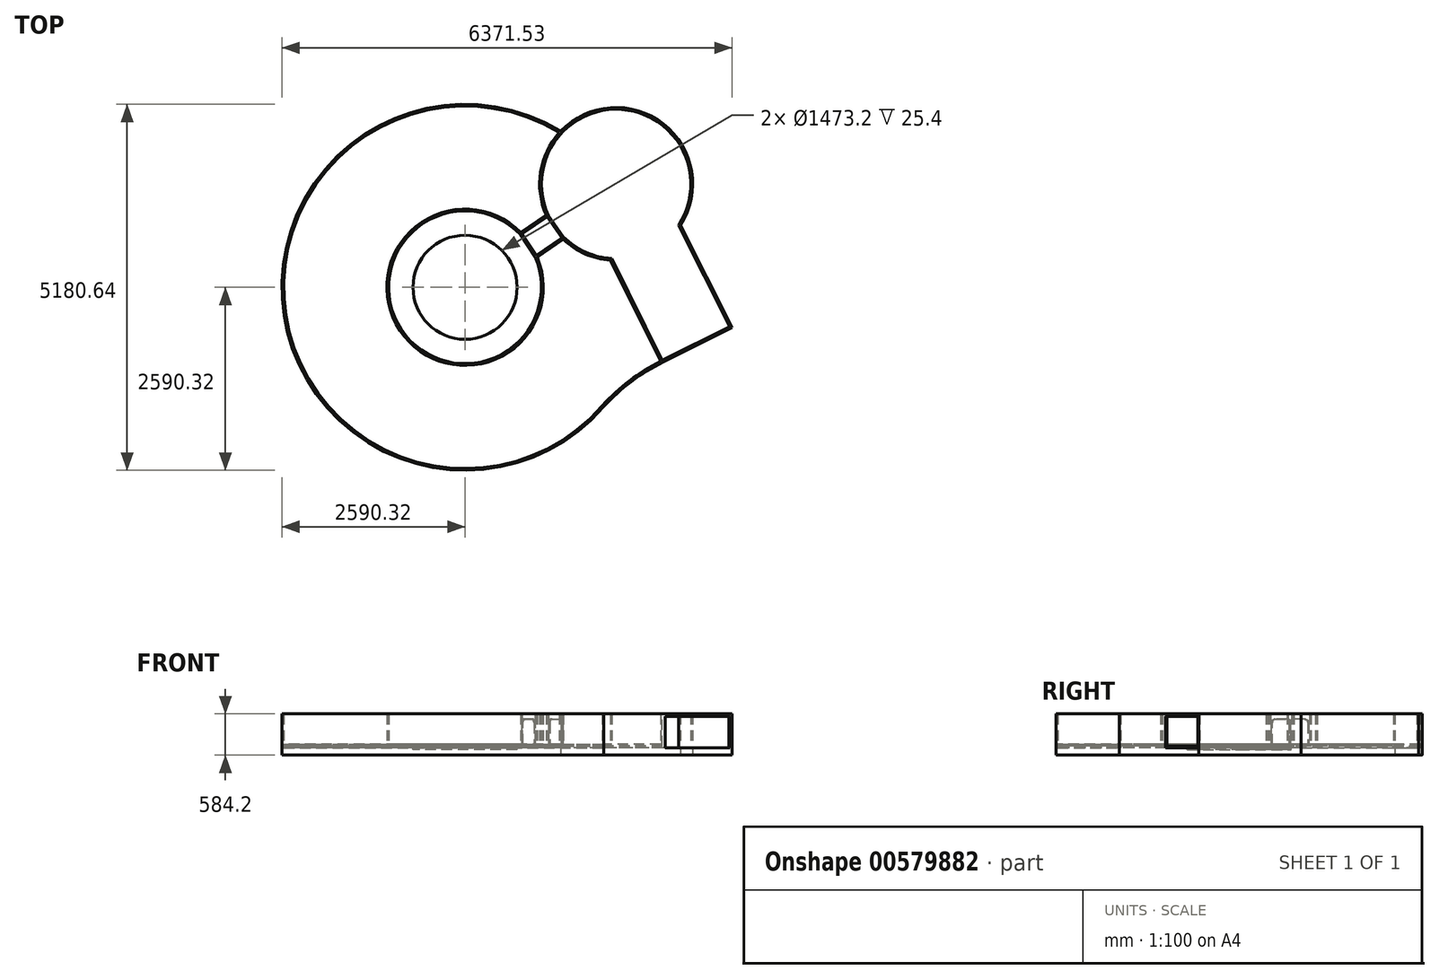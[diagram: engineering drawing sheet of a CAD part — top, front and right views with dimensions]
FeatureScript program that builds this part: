
annotation { "Feature Type Name" : "Feature", "Feature Type Description" : "" }
export const myFeature = defineFeature(function(context is Context, id is Id, definition is map)
    precondition{}
    {
        {
            var Q0;
            Q0=qCreatedBy(makeId("Top.planeOp"),FACE);
            var sketch = newSketch(context, id + "F0", { "sketchPlane" : qUnion([Q0])});
            skArc(sketch, "E0", {"start": v(1353.94, 2208.3) * mm, "mid": v(-2559.24, -400.08) * mm, "end": v(1963.3, -1689.73) * mm});
            skArc(sketch, "E1", {"start": v(1393.84, 711.58) * mm, "mid": v(1706.32, 497.31) * mm, "end": v(2074.27, 407) * mm});
            skLineSegment(sketch, "E2.0", {"start": v(2085.56, 384.25) * mm, "end": v(2789.38, -1035.12) * mm});
            skLineSegment(sketch, "E3.0", {"start": v(3031.93, 857.23) * mm, "end": v(3747.03, -556.58) * mm});
            skLineSegment(sketch, "E4", {"start": v(3781.21, -567.89) * mm, "end": v(2800.66, -1057.88) * mm});
            skArc(sketch, "E5", {"start": v(2800.66, -1057.88) * mm, "mid": v(2353, -1335.39) * mm, "end": v(1963.3, -1689.73) * mm});
            skCircle(sketch, "E6", {"center": v(0, 0) * mm, "radius": 762 * mm});
            skArc(sketch, "E7", {"start": v(786.05, 742.15) * mm, "mid": v(-901.05, -597.29) * mm, "end": v(989.68, 434.94) * mm});
            skLineSegment(sketch, "E8", {"start": v(-1106.44, 0) * mm, "end": v(-2564.92, 0) * mm});
            skLineSegment(sketch, "E9", {"start": v(0, 1106.44) * mm, "end": v(0, 2564.92) * mm});
            skLineSegment(sketch, "E10", {"start": v(0, -1106.44) * mm, "end": v(0, -2564.92) * mm});
            skLineSegment(sketch, "E11.0", {"start": v(1160.51, 998.22) * mm, "end": v(807.27, 756.66) * mm});
            skLineSegment(sketch, "E12.0", {"start": v(1372.87, 697.23) * mm, "end": v(1011, 449.54) * mm});
            skLineSegment(sketch, "E13", {"start": v(786.05, 742.15) * mm, "end": v(989.68, 434.94) * mm});
            skLineSegment(sketch, "E14", {"start": v(1181.48, 1012.56) * mm, "end": v(1393.84, 711.58) * mm});
            skArc(sketch, "E15.trimOffspring", {"start": v(3020.47, 879.9) * mm, "mid": v(2214.25, 2516.5) * mm, "end": v(1181.48, 1012.56) * mm});
            skLineSegment(sketch, "E16", {"start": v(2074.27, 407) * mm, "end": v(3020.47, 879.9) * mm});
            skCircle(sketch, "E17.0", {"center": v(0, 0) * mm, "radius": 736.6 * mm});
            skLineSegment(sketch, "E18.0", {"start": v(1149.48, 1021.44) * mm, "end": v(789.44, 775.24) * mm});
            skArc(sketch, "E18.1", {"start": v(3049.74, 878.31) * mm, "mid": v(2806.23, 2313.93) * mm, "end": v(1353.94, 2208.3) * mm});
            skLineSegment(sketch, "E19.0", {"start": v(1391.03, 678.87) * mm, "end": v(1021.24, 425.76) * mm});
            skArc(sketch, "E19.1", {"start": v(1391.03, 678.87) * mm, "mid": v(1698.8, 472.86) * mm, "end": v(2058, 382.64) * mm});
            skArc(sketch, "E20.1", {"start": v(2766.7, -1046.58) * mm, "mid": v(2327.45, -1322.88) * mm, "end": v(1944.3, -1672.87) * mm});
            skLineSegment(sketch, "E20.2", {"start": v(2058, 382.64) * mm, "end": v(2766.7, -1046.58) * mm});
            skLineSegment(sketch, "E21.0", {"start": v(3747.14, -556.52) * mm, "end": v(2789.3, -1035.16) * mm});
            skArc(sketch, "E22.trimOffspring", {"start": v(789.44, 775.24) * mm, "mid": v(-922.05, -611.58) * mm, "end": v(1021.24, 425.76) * mm});
            skLineSegment(sketch, "E23", {"start": v(807.27, 756.66) * mm, "end": v(1011, 449.54) * mm});
            skLineSegment(sketch, "E24.0", {"start": v(1160.73, 997.91) * mm, "end": v(1373.08, 696.93) * mm});
            skLineSegment(sketch, "E25", {"start": v(1160.73, 997.91) * mm, "end": v(1160.51, 998.22) * mm});
            skArc(sketch, "E26.trimOffspring", {"start": v(1336.3, 2189.32) * mm, "mid": v(-2533.72, -398.87) * mm, "end": v(1944.3, -1672.87) * mm});
            skArc(sketch, "E27.trimOffspring", {"start": v(1336.3, 2189.32) * mm, "mid": v(1069.3, 1633.15) * mm, "end": v(1149.48, 1021.44) * mm});
            skPoint(sketch, "E28.orphan", {"position": v(0, 1081.04) * mm});
            skPoint(sketch, "E29.orphan", {"position": v(-1081.04, 0) * mm});
            skPoint(sketch, "E30.orphan", {"position": v(0, -1081.04) * mm});
            skLineSegment(sketch, "E31.0", {"start": v(2085.63, 384.28) * mm, "end": v(3031.83, 857.18) * mm});
            skLineSegment(sketch, "E32", {"start": v(2085.63, 384.28) * mm, "end": v(2085.56, 384.25) * mm});
            skLineSegment(sketch, "E33", {"start": v(3031.83, 857.18) * mm, "end": v(3031.93, 857.23) * mm});
            skLineSegment(sketch, "E34", {"start": v(2766.7, -1046.58) * mm, "end": v(2789.38, -1035.12) * mm});
            skLineSegment(sketch, "E35", {"start": v(1181.48, 1012.56) * mm, "end": v(1149.48, 1021.44) * mm});
            skLineSegment(sketch, "E36", {"start": v(3049.74, 878.31) * mm, "end": v(3781.21, -567.89) * mm});
            skSolve(sketch);
        }
        {
            var Q0;
            Q0=makeQuery(id+"F0.imprint","IMPRINT",FACE,{"disambiguationData":[TD([[makeQuery(id+"F0.imprint","IMPRINT",EDGE,{"derivedFrom":sQuery(id+"F0.wireOp",EDGE,"E0")}),1.0]])]});
            var sketch = newSketch(context, id + "F1", { "sketchPlane" : qUnion([Q0])});
            skArc(sketch, "E37.0", {"start": v(1353.94, 2208.3) * mm, "mid": v(-2559.24, -400.08) * mm, "end": v(1963.3, -1689.73) * mm});
            skArc(sketch, "E38.0", {"start": v(2800.66, -1057.88) * mm, "mid": v(2353, -1335.39) * mm, "end": v(1963.3, -1689.73) * mm});
            skLineSegment(sketch, "E39.0", {"start": v(3781.21, -567.89) * mm, "end": v(2800.66, -1057.88) * mm});
            skLineSegment(sketch, "E40.0", {"start": v(3049.74, 878.31) * mm, "end": v(3781.21, -567.89) * mm});
            skArc(sketch, "E41.0", {"start": v(3049.74, 878.31) * mm, "mid": v(2806.23, 2313.93) * mm, "end": v(1353.94, 2208.3) * mm});
            skSolve(sketch);
        }
        {
            var Q0;
            Q0=makeQuery(id+"F0.imprint","IMPRINT",FACE,{"disambiguationData":[TD([[makeQuery(id+"F0.imprint","IMPRINT",EDGE,{"derivedFrom":sQuery(id+"F0.wireOp",EDGE,"E0")}),1.0]])]});
            var sketch = newSketch(context, id + "F2", { "sketchPlane" : qUnion([Q0])});
            skLineSegment(sketch, "E42.0.0", {"start": v(2800.66, -1057.88) * mm, "end": v(3781.21, -567.89) * mm});
            skLineSegment(sketch, "E42.0.1", {"start": v(3781.21, -567.89) * mm, "end": v(3049.74, 878.31) * mm});
            skArc(sketch, "E42.0.2", {"start": v(3049.74, 878.31) * mm, "mid": v(2806.23, 2313.93) * mm, "end": v(1353.94, 2208.3) * mm});
            skArc(sketch, "E42.0.3", {"start": v(1353.94, 2208.3) * mm, "mid": v(-2559.24, -400.08) * mm, "end": v(1963.3, -1689.73) * mm});
            skArc(sketch, "E42.0.4", {"start": v(1963.3, -1689.73) * mm, "mid": v(2353, -1335.39) * mm, "end": v(2800.66, -1057.88) * mm});
            skCircle(sketch, "E43.0.0", {"center": v(0, 0) * mm, "radius": 762 * mm});
            skCircle(sketch, "E44.0", {"center": v(0, 0) * mm, "radius": 736.6 * mm});
            skArc(sketch, "E45.0", {"start": v(786.05, 742.15) * mm, "mid": v(-901.05, -597.29) * mm, "end": v(989.68, 434.94) * mm});
            skArc(sketch, "E46.0", {"start": v(789.44, 775.24) * mm, "mid": v(-922.05, -611.58) * mm, "end": v(1021.24, 425.76) * mm});
            skLineSegment(sketch, "E47.0.0", {"start": v(1372.87, 697.23) * mm, "end": v(1160.73, 997.91) * mm});
            skLineSegment(sketch, "E47.0.1", {"start": v(1160.73, 997.91) * mm, "end": v(1160.51, 998.22) * mm});
            skLineSegment(sketch, "E47.0.2", {"start": v(1160.51, 998.22) * mm, "end": v(807.27, 756.66) * mm});
            skLineSegment(sketch, "E47.0.3", {"start": v(807.27, 756.66) * mm, "end": v(1011, 449.54) * mm});
            skLineSegment(sketch, "E47.0.4", {"start": v(1011, 449.54) * mm, "end": v(1372.87, 697.23) * mm});
            skLineSegment(sketch, "E47.1", {"start": v(786.05, 742.15) * mm, "end": v(989.68, 434.94) * mm});
            skLineSegment(sketch, "E48.0", {"start": v(1149.48, 1021.44) * mm, "end": v(789.44, 775.24) * mm});
            skLineSegment(sketch, "E48.1", {"start": v(1391.03, 678.87) * mm, "end": v(1021.24, 425.76) * mm});
            skLineSegment(sketch, "E48.2", {"start": v(1181.48, 1012.56) * mm, "end": v(1393.84, 711.58) * mm});
            skPoint(sketch, "E48.3", {"position": v(1287.66, 862.07) * mm});
            skArc(sketch, "E49.0", {"start": v(1336.3, 2189.32) * mm, "mid": v(1069.3, 1633.15) * mm, "end": v(1149.48, 1021.44) * mm});
            skArc(sketch, "E50.0", {"start": v(3020.47, 879.9) * mm, "mid": v(2214.25, 2516.5) * mm, "end": v(1181.48, 1012.56) * mm});
            skArc(sketch, "E51.0", {"start": v(1393.84, 711.58) * mm, "mid": v(1706.32, 497.31) * mm, "end": v(2074.27, 407) * mm});
            skArc(sketch, "E52.0", {"start": v(1391.03, 678.87) * mm, "mid": v(1698.8, 472.86) * mm, "end": v(2058, 382.64) * mm});
            skArc(sketch, "E53.0", {"start": v(1336.3, 2189.32) * mm, "mid": v(-2533.72, -398.87) * mm, "end": v(1944.3, -1672.87) * mm});
            skArc(sketch, "E54.0", {"start": v(2766.7, -1046.58) * mm, "mid": v(2327.45, -1322.88) * mm, "end": v(1944.3, -1672.87) * mm});
            skLineSegment(sketch, "E55.0", {"start": v(2058, 382.64) * mm, "end": v(2766.7, -1046.58) * mm});
            skLineSegment(sketch, "E56.0", {"start": v(2085.56, 384.25) * mm, "end": v(2789.38, -1035.12) * mm});
            skLineSegment(sketch, "E57.0", {"start": v(3031.93, 857.23) * mm, "end": v(3747.03, -556.58) * mm});
            skLineSegment(sketch, "E58.0", {"start": v(3747.14, -556.52) * mm, "end": v(2789.3, -1035.16) * mm});
            skLineSegment(sketch, "E59", {"start": v(2085.63, 384.28) * mm, "end": v(2074.27, 407) * mm});
            skLineSegment(sketch, "E60", {"start": v(3020.47, 879.9) * mm, "end": v(3031.93, 857.23) * mm});
            skPoint(sketch, "E61.0.end.orphan", {"position": v(3031.83, 857.18) * mm});
            skPoint(sketch, "E62.0.end.orphan", {"position": v(3020.47, 879.9) * mm});
            skPoint(sketch, "E62.0.start.orphan", {"position": v(2074.27, 407) * mm});
            skSolve(sketch);
        }
        {
            var Q0;
            Q0 = qSketchRegion(id + "F1", true);
            extrude(context, id + "F3", {"entities" : qUnion([Q0]), "depth" : 76.2 * mm, "offsetDistance" : 25.4 * mm});
        }
        {
            var Q0;
            Q0 = qSketchRegion(id + "F2", true);
            extrude(context, id + "F4", {"entities" : qUnion([Q0]), "operationType" : NewBodyOperationType.ADD, "depth" : 508 * mm, "offsetDistance" : 25.4 * mm});
        }
        {
            var Q0;
            Q0=makeQuery(id+"F4.opExtrude","CAP_FACE",FACE,{"disambiguationData":[OSD([sQuery(id+"F2.wireOp",EDGE,"E42.0.0"),sQuery(id+"F2.wireOp",EDGE,"E42.0.1"),sQuery(id+"F2.wireOp",EDGE,"E42.0.2"),sQuery(id+"F2.wireOp",EDGE,"E42.0.3"),sQuery(id+"F2.wireOp",EDGE,"E42.0.4"),sQuery(id+"F2.wireOp",EDGE,"E45.0"),sQuery(id+"F2.wireOp",EDGE,"E46.0"),sQuery(id+"F2.wireOp",EDGE,"E47.0.0"),sQuery(id+"F2.wireOp",EDGE,"E47.0.1"),sQuery(id+"F2.wireOp",EDGE,"E47.0.2"),sQuery(id+"F2.wireOp",EDGE,"E47.0.3"),sQuery(id+"F2.wireOp",EDGE,"E47.0.4"),sQuery(id+"F2.wireOp",EDGE,"E47.1"),sQuery(id+"F2.wireOp",EDGE,"E48.0"),sQuery(id+"F2.wireOp",EDGE,"E48.1"),sQuery(id+"F2.wireOp",EDGE,"E48.2"),sQuery(id+"F2.wireOp",EDGE,"E49.0"),sQuery(id+"F2.wireOp",EDGE,"E50.0"),sQuery(id+"F2.wireOp",EDGE,"E51.0"),sQuery(id+"F2.wireOp",EDGE,"E52.0"),sQuery(id+"F2.wireOp",EDGE,"E62.0"),sQuery(id+"F2.wireOp",EDGE,"E53.0"),sQuery(id+"F2.wireOp",EDGE,"E54.0"),sQuery(id+"F2.wireOp",EDGE,"E55.0")])],"isStart":false});
            shell(context, id + "F5", {"entities" : qUnion([Q0]), "thickness" : 25.4 * mm});
        }
        {
            var Q0;
            Q0=makeQuery(id+"F4.opExtrude","SWEPT_FACE",FACE,{"disambiguationData":[OSD([sQuery(id+"F2.wireOp",EDGE,"E47.1")])]});
            var sketch = newSketch(context, id + "F6", { "sketchPlane" : qUnion([Q0])});
            skLineSegment(sketch, "E63.0", {"start": v(-184.28, 508) * mm, "end": v(-184.28, 76.2) * mm});
            skLineSegment(sketch, "E64.0", {"start": v(184.28, 508) * mm, "end": v(184.28, 76.2) * mm});
            skLineSegment(sketch, "E65.0", {"start": v(-158.88, 381) * mm, "end": v(-158.88, 76.2) * mm});
            skLineSegment(sketch, "E66.0", {"start": v(158.88, 381) * mm, "end": v(158.88, 76.2) * mm});
            skPoint(sketch, "E67.0", {"position": v(0, 508) * mm});
            skLineSegment(sketch, "E68.0", {"start": v(-184.28, 508) * mm, "end": v(184.28, 508) * mm});
            skLineSegment(sketch, "E69.0", {"start": v(-108.08, 431.8) * mm, "end": v(108.08, 431.8) * mm});
            skArc(sketch, "E70", {"start": v(-108.08, 431.8) * mm, "mid": v(-144, 416.92) * mm, "end": v(-158.88, 381) * mm});
            skArc(sketch, "E71", {"start": v(158.88, 381) * mm, "mid": v(144, 416.92) * mm, "end": v(108.08, 431.8) * mm});
            skLineSegment(sketch, "E72.0", {"start": v(158.88, 76.2) * mm, "end": v(-158.88, 76.2) * mm});
            skSolve(sketch);
        }
        {
            var Q0;
            Q0=makeQuery(id+"F6.imprint","IMPRINT",FACE,{"disambiguationData":[TD([[makeQuery(id+"F6.imprint","IMPRINT",EDGE,{"derivedFrom":sQuery(id+"F6.wireOp",EDGE,"E65.0")}),1.0]])]});
            extrude(context, id + "F7", {"entities" : qUnion([Q0]), "operationType" : NewBodyOperationType.REMOVE, "oppositeDirection" : true, "depth" : 1125.22 * mm, "offsetDistance" : 25.4 * mm});
        }
        {
            var Q0;
            Q0=makeQuery(id+"F4.boolean.opBoolean","MERGE",FACE,{"derivedFrom":[makeQuery(id+"F3.opExtrude","SWEPT_FACE",FACE,{"disambiguationData":[OSD([sQuery(id+"F1.wireOp",EDGE,"E39.0")])]}),makeQuery(id+"F4.opExtrude","SWEPT_FACE",FACE,{"disambiguationData":[OSD([sQuery(id+"F2.wireOp",EDGE,"E42.0.0")])]})]});
            var sketch = newSketch(context, id + "F8", { "sketchPlane" : qUnion([Q0])});
            skLineSegment(sketch, "E73.0", {"start": v(2070.5, 469.9) * mm, "end": v(2070.5, 0) * mm});
            skLineSegment(sketch, "E73.1", {"start": v(3090.46, 469.9) * mm, "end": v(2070.5, 469.9) * mm});
            skLineSegment(sketch, "E73.2", {"start": v(3090.46, 469.9) * mm, "end": v(3090.46, 0) * mm});
            skLineSegment(sketch, "E74.0", {"start": v(3103.16, 0) * mm, "end": v(2032.4, 0) * mm});
            skLineSegment(sketch, "E75.0.0", {"start": v(2032.4, 0) * mm, "end": v(3128.56, 0) * mm});
            skLineSegment(sketch, "E75.0.1", {"start": v(3128.56, 0) * mm, "end": v(3128.56, 508) * mm});
            skLineSegment(sketch, "E75.0.2", {"start": v(3128.56, 508) * mm, "end": v(2032.4, 508) * mm});
            skLineSegment(sketch, "E75.0.3", {"start": v(2032.4, 508) * mm, "end": v(2032.4, 0) * mm});
            skLineSegment(sketch, "E76.0", {"start": v(2032.4, 25.4) * mm, "end": v(3128.56, 25.4) * mm});
            skSolve(sketch);
        }
        {
            var Q0;
            {var subQ0=sQuery(id+"F8.wireOp",EDGE,"E73.1");Q0=makeQuery(id+"F8.imprint","IMPRINT",FACE,{"disambiguationData":[TD([[makeQuery(id+"F8.imprint","IMPRINT",EDGE,{"derivedFrom":subQ0}),1.0]])]});}
            extrude(context, id + "F9", {"entities" : qUnion([Q0]), "operationType" : NewBodyOperationType.REMOVE, "oppositeDirection" : true, "depth" : 25.4 * mm, "offsetDistance" : 25.4 * mm});
        }
        {
            var Q0;
            {var subQ0=makeQuery(id+"F3.opExtrude","CAP_FACE",FACE,{"disambiguationData":[OSD([sQuery(id+"F1.wireOp",EDGE,"E37.0"),sQuery(id+"F1.wireOp",EDGE,"E38.0"),sQuery(id+"F1.wireOp",EDGE,"E39.0"),sQuery(id+"F1.wireOp",EDGE,"E40.0"),sQuery(id+"F1.wireOp",EDGE,"E41.0")])],"isStart":false});Q0=makeQuery(id+"F7.boolean.opBoolean","MERGE",FACE,{"derivedFrom":[makeQuery(id+"F4.boolean.opBoolean","SPLIT",FACE,{"disambiguationData":[TD([makeQuery(id+"F4.opExtrude","SWEPT_FACE",FACE,{"disambiguationData":[OSD([sQuery(id+"F2.wireOp",EDGE,"E45.0")])]})])],"derivedFrom":subQ0}),makeQuery(id+"F4.boolean.opBoolean","SPLIT",FACE,{"disambiguationData":[TD([makeQuery(id+"F4.opExtrude","SWEPT_FACE",FACE,{"disambiguationData":[OSD([sQuery(id+"F2.wireOp",EDGE,"E47.0.2")])]})])],"derivedFrom":subQ0}),makeQuery(id+"F7.opExtrude","SWEPT_FACE",FACE,{"disambiguationData":[OSD([sQuery(id+"F6.wireOp",EDGE,"E72.0")])]})]});}
            var sketch = newSketch(context, id + "F10", { "sketchPlane" : qUnion([Q0])});
            skCircle(sketch, "E77.0", {"center": v(0, 0) * mm, "radius": 736.6 * mm});
            skSolve(sketch);
        }
        {
            var Q0;
            Q0=makeQuery(id+"F10.imprint","IMPRINT",FACE,{"disambiguationData":[TD([[makeQuery(id+"F10.imprint","IMPRINT",EDGE,{"derivedFrom":sQuery(id+"F10.wireOp",EDGE,"E77.0")}),1.0]])]});
            extrude(context, id + "F11", {"entities" : qUnion([Q0]), "operationType" : NewBodyOperationType.REMOVE, "oppositeDirection" : true, "depth" : 76.2 * mm, "offsetDistance" : 25.4 * mm});
        }
        {
            var Q0;
            Q0=makeQuery(id+"F0.imprint","IMPRINT",FACE,{"disambiguationData":[TD([[makeQuery(id+"F0.imprint","IMPRINT",EDGE,{"derivedFrom":sQuery(id+"F0.wireOp",EDGE,"E0")}),1.0]])]});
            var sketch = newSketch(context, id + "F12", { "sketchPlane" : qUnion([Q0])});
            skArc(sketch, "E78.0", {"start": v(1353.94, 2208.3) * mm, "mid": v(-2559.24, -400.08) * mm, "end": v(1963.3, -1689.73) * mm});
            skArc(sketch, "E79.0", {"start": v(3049.74, 878.31) * mm, "mid": v(2806.23, 2313.93) * mm, "end": v(1353.94, 2208.3) * mm});
            skLineSegment(sketch, "E80.0", {"start": v(3049.74, 878.31) * mm, "end": v(3781.21, -567.89) * mm});
            skLineSegment(sketch, "E81.0", {"start": v(3781.21, -567.89) * mm, "end": v(2800.66, -1057.88) * mm});
            skArc(sketch, "E82.0", {"start": v(2800.66, -1057.88) * mm, "mid": v(2353, -1335.39) * mm, "end": v(1963.3, -1689.73) * mm});
            skSolve(sketch);
        }
        {
            var Q0;
            Q0 = qSketchRegion(id + "F12", true);
            extrude(context, id + "F13", {"entities" : qUnion([Q0]), "operationType" : NewBodyOperationType.ADD, "oppositeDirection" : true, "depth" : 76.2 * mm, "offsetDistance" : 25.4 * mm});
        }
    });
